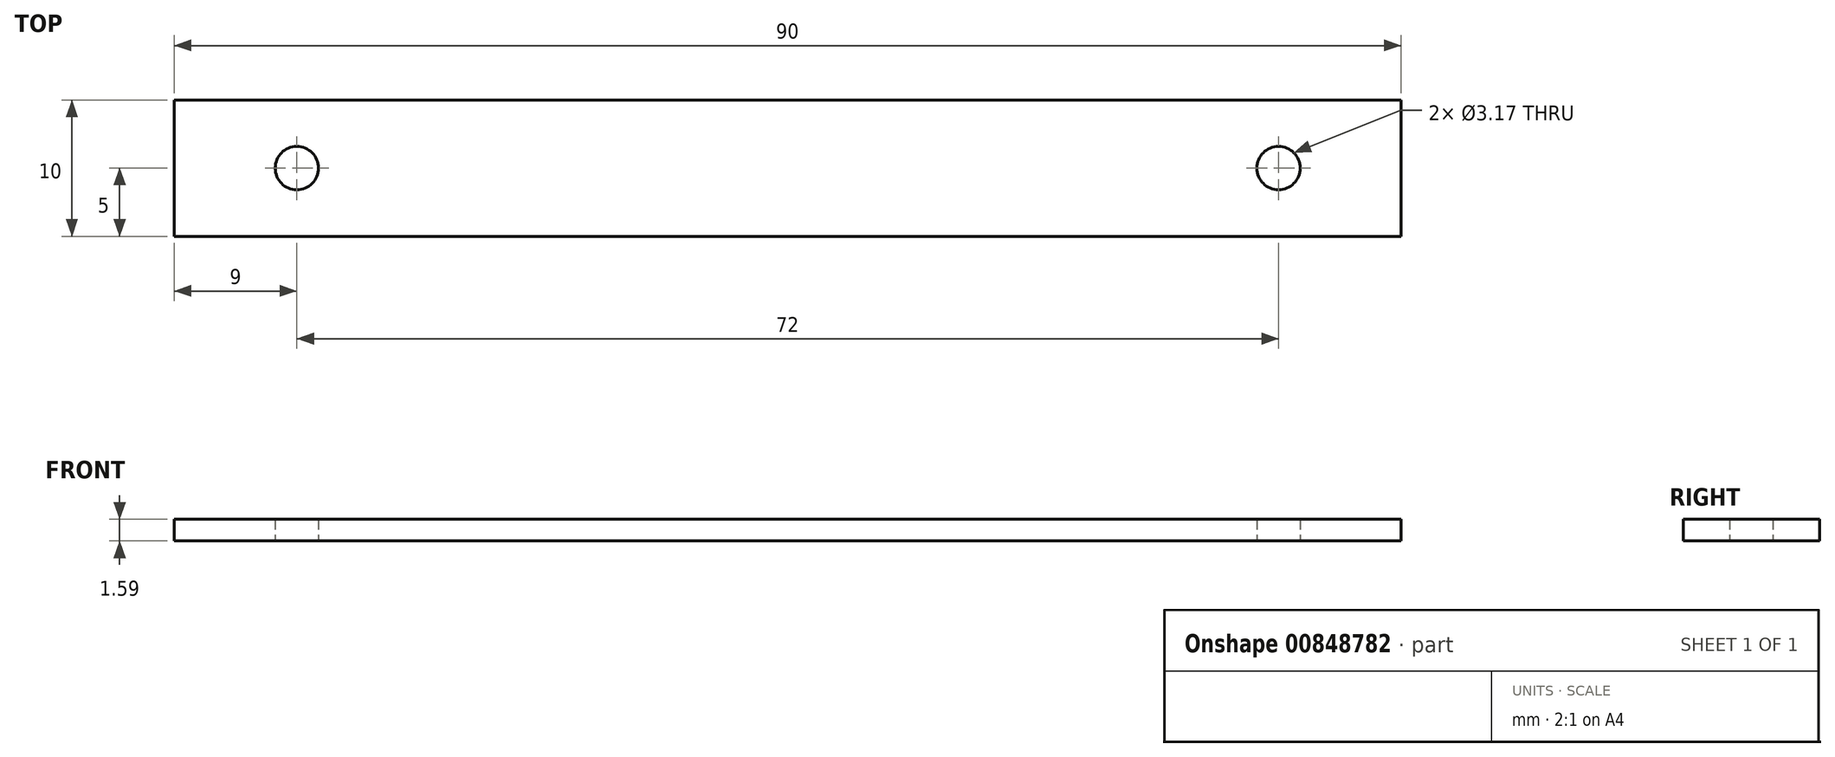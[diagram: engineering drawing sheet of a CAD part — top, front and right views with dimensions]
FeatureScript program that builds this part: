
annotation { "Feature Type Name" : "Feature", "Feature Type Description" : "" }
export const myFeature = defineFeature(function(context is Context, id is Id, definition is map)
    precondition{}
    {
        {
            var Q0;
            Q0=qCreatedBy(makeId("Top.planeOp"),FACE);
            var sketch = newSketch(context, id + "F0", { "sketchPlane" : qUnion([Q0])});
            skLineSegment(sketch, "E0.bottom", {"start": v(-45, 0) * mm, "end": v(45, 0) * mm});
            skLineSegment(sketch, "E0.top", {"start": v(-45, -10) * mm, "end": v(45, -10) * mm});
            skLineSegment(sketch, "E0.left", {"start": v(-45, 0) * mm, "end": v(-45, -10) * mm});
            skLineSegment(sketch, "E0.right", {"start": v(45, 0) * mm, "end": v(45, -10) * mm});
            skCircle(sketch, "E1", {"center": v(-36, -5) * mm, "radius": 1.59 * mm});
            skPoint(sketch, "E1.centerSnap0", {"position": v(-45, -5) * mm});
            skCircle(sketch, "E2.MirrorC", {"center": v(36, -5) * mm, "radius": 1.59 * mm});
            skSolve(sketch);
        }
        {
            var Q0;
            Q0 = qSketchRegion(id + "F0", true);
            extrude(context, id + "F1", {"entities" : qUnion([Q0]), "depth" : 1.59 * mm, "offsetDistance" : 25 * mm});
        }
    });
